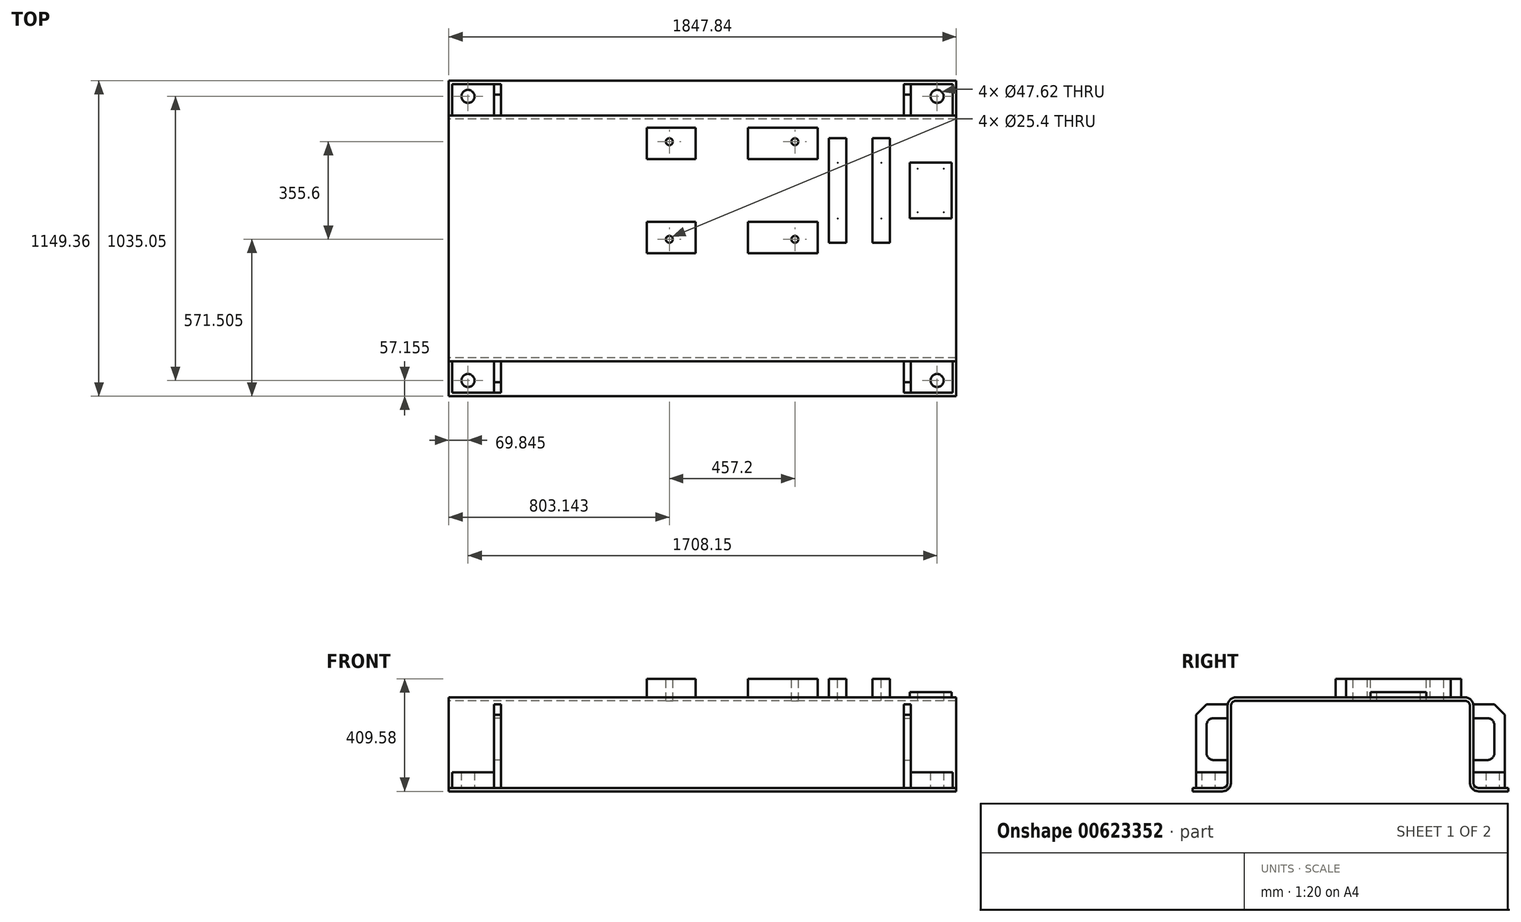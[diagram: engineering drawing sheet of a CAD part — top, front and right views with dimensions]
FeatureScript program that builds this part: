
annotation { "Feature Type Name" : "Feature", "Feature Type Description" : "" }
export const myFeature = defineFeature(function(context is Context, id is Id, definition is map)
    precondition{}
    {
        {
            var Q0;
            Q0=qCreatedBy(makeId("Right.planeOp"),FACE);
            var sketch = newSketch(context, id + "F0", { "sketchPlane" : qUnion([Q0])});
            skLineSegment(sketch, "E0.bottom", {"start": v(-415.93, 171.45) * mm, "end": v(0, 171.45) * mm});
            skLineSegment(sketch, "E0.top", {"start": v(-574.68, -171.45) * mm, "end": v(-466.73, -171.45) * mm});
            skLineSegment(sketch, "E0.left", {"start": v(-574.68, -158.75) * mm, "end": v(-574.68, -171.45) * mm});
            skPoint(sketch, "E0.middle", {"position": v(0, 0) * mm});
            skLineSegment(sketch, "E1", {"start": v(0, 352.56) * mm, "end": v(0, -350.8) * mm, "construction": true});
            skPoint(sketch, "E1.endSnap0", {"position": v(0, 171.45) * mm});
            skLineSegment(sketch, "E2.0", {"start": v(-447.68, 139.7) * mm, "end": v(-447.68, -139.7) * mm});
            skLineSegment(sketch, "E3.0", {"start": v(-574.68, -158.75) * mm, "end": v(-466.73, -158.75) * mm});
            skLineSegment(sketch, "E4.0", {"start": v(-434.98, 139.7) * mm, "end": v(-434.98, -139.7) * mm});
            skLineSegment(sketch, "E5.0", {"start": v(-415.93, 158.75) * mm, "end": v(0, 158.75) * mm});
            skArc(sketch, "E6.filletArc", {"start": v(-466.73, -158.75) * mm, "mid": v(-453.25, -153.17) * mm, "end": v(-447.68, -139.7) * mm});
            skArc(sketch, "E7.filletArc", {"start": v(-415.93, 158.75) * mm, "mid": v(-429.4, 153.17) * mm, "end": v(-434.98, 139.7) * mm});
            skPoint(sketch, "E8.newPointA", {"position": v(574.68, -171.45) * mm});
            skArc(sketch, "E8.filletArc", {"start": v(-466.73, -171.45) * mm, "mid": v(-444.27, -162.15) * mm, "end": v(-434.98, -139.7) * mm});
            skPoint(sketch, "E9.newPointB", {"position": v(-574.67, 171.45) * mm});
            skArc(sketch, "E9.filletArc", {"start": v(-415.93, 171.45) * mm, "mid": v(-438.38, 162.15) * mm, "end": v(-447.68, 139.7) * mm});
            skArc(sketch, "E10.MirrorCS", {"start": v(466.73, -158.75) * mm, "mid": v(453.25, -153.17) * mm, "end": v(447.68, -139.7) * mm});
            skArc(sketch, "E11.MirrorCS", {"start": v(415.93, 158.75) * mm, "mid": v(429.4, 153.17) * mm, "end": v(434.98, 139.7) * mm});
            skLineSegment(sketch, "E12.MirrorCS", {"start": v(574.68, -158.75) * mm, "end": v(574.68, -171.45) * mm});
            skArc(sketch, "E13.MirrorCS", {"start": v(466.73, -171.45) * mm, "mid": v(444.27, -162.15) * mm, "end": v(434.98, -139.7) * mm});
            skArc(sketch, "E14.MirrorCS", {"start": v(415.93, 171.45) * mm, "mid": v(438.38, 162.15) * mm, "end": v(447.68, 139.7) * mm});
            skLineSegment(sketch, "E15.MirrorCS", {"start": v(574.68, -171.45) * mm, "end": v(466.73, -171.45) * mm});
            skLineSegment(sketch, "E16.MirrorCS", {"start": v(574.68, -158.75) * mm, "end": v(466.73, -158.75) * mm});
            skPoint(sketch, "E17.MirrorP", {"position": v(574.68, 171.45) * mm});
            skLineSegment(sketch, "E18.MirrorCS", {"start": v(447.68, 139.7) * mm, "end": v(447.68, -139.7) * mm});
            skLineSegment(sketch, "E19.MirrorCS", {"start": v(434.98, 139.7) * mm, "end": v(434.98, -139.7) * mm});
            skLineSegment(sketch, "E20.MirrorCS", {"start": v(415.93, 158.75) * mm, "end": v(0, 158.75) * mm});
            skLineSegment(sketch, "E21.MirrorCS", {"start": v(415.93, 171.45) * mm, "end": v(0, 171.45) * mm});
            skSolve(sketch);
        }
        {
            var Q0;
            Q0 = qSketchRegion(id + "F0", true);
            extrude(context, id + "F1", {"entities" : qUnion([Q0]), "endBound" : BoundingType.SYMMETRIC, "depth" : 1847.85 * mm, "offsetDistance" : 25.4 * mm});
        }
        {
            var Q0;
            Q0=makeQuery(id+"F1.opExtrude","SWEPT_FACE",FACE,{"disambiguationData":[OSD([sQuery(id+"F0.wireOp",EDGE,"E3.0")])]});
            var sketch = newSketch(context, id + "F2", { "sketchPlane" : qUnion([Q0])});
            skLineSegment(sketch, "E22.0", {"start": v(911.23, -561.98) * mm, "end": v(911.23, -447.68) * mm});
            skLineSegment(sketch, "E23.0", {"start": v(758.83, -561.98) * mm, "end": v(758.83, -447.68) * mm});
            skLineSegment(sketch, "E24.0", {"start": v(923.93, -447.68) * mm, "end": v(758.83, -447.68) * mm});
            skLineSegment(sketch, "E25.0.1", {"start": v(758.83, -447.68) * mm, "end": v(923.93, -447.68) * mm});
            skLineSegment(sketch, "E26.0", {"start": v(911.23, -447.68) * mm, "end": v(758.83, -447.68) * mm});
            skLineSegment(sketch, "E27.0", {"start": v(911.23, -561.98) * mm, "end": v(758.83, -561.98) * mm});
            skPoint(sketch, "E28.orphan", {"position": v(-923.93, -447.68) * mm});
            skLineSegment(sketch, "E29", {"start": v(0, 247.47) * mm, "end": v(0, -268.79) * mm, "construction": true});
            skLineSegment(sketch, "E30", {"start": v(-290.88, 0) * mm, "end": v(261.25, 0) * mm, "construction": true});
            skLineSegment(sketch, "E31.0", {"start": v(854.08, 247.47) * mm, "end": v(854.08, -517.52) * mm, "construction": true});
            skLineSegment(sketch, "E32.0", {"start": v(-290.88, -517.52) * mm, "end": v(854.08, -517.52) * mm, "construction": true});
            skCircle(sketch, "E33", {"center": v(854.08, -517.52) * mm, "radius": 23.81 * mm});
            skSolve(sketch);
        }
        {
            var Q0;
            Q0 = qSketchRegion(id + "F2", true);
            extrude(context, id + "F3", {"entities" : qUnion([Q0]), "depth" : 57.15 * mm, "offsetDistance" : 25.4 * mm});
        }
        {
            var Q0;
            Q0=makeQuery(id+"F3.opExtrude","SWEPT_FACE",FACE,{"disambiguationData":[OSD([sQuery(id+"F2.wireOp",EDGE,"E23.0")])]});
            var sketch = newSketch(context, id + "F4", { "sketchPlane" : qUnion([Q0])});
            skLineSegment(sketch, "E34.bottom", {"start": v(447.68, -158.75) * mm, "end": v(561.98, -158.75) * mm});
            skLineSegment(sketch, "E34.top", {"start": v(447.67, 146.05) * mm, "end": v(561.98, 146.05) * mm});
            skLineSegment(sketch, "E34.left", {"start": v(447.68, -158.75) * mm, "end": v(447.68, -57.15) * mm});
            skLineSegment(sketch, "E34.right", {"start": v(561.98, -158.75) * mm, "end": v(561.98, 146.05) * mm});
            skLineSegment(sketch, "E35.0", {"start": v(447.67, 95.25) * mm, "end": v(498.48, 95.25) * mm});
            skLineSegment(sketch, "E36.0", {"start": v(447.67, -57.15) * mm, "end": v(498.48, -57.15) * mm});
            skLineSegment(sketch, "E37.0", {"start": v(523.88, -31.75) * mm, "end": v(523.88, 69.85) * mm});
            skArc(sketch, "E38.filletArc", {"start": v(523.88, 69.85) * mm, "mid": v(516.44, 87.81) * mm, "end": v(498.48, 95.25) * mm});
            skArc(sketch, "E39.filletArc", {"start": v(498.48, -57.15) * mm, "mid": v(516.44, -49.71) * mm, "end": v(523.88, -31.75) * mm});
            skLineSegment(sketch, "E40.trimOffspring", {"start": v(447.68, 95.25) * mm, "end": v(447.68, 146.05) * mm});
            skSolve(sketch);
        }
        {
            var Q0;
            Q0 = qSketchRegion(id + "F4", true);
            extrude(context, id + "F5", {"entities" : qUnion([Q0]), "depth" : 25.4 * mm, "offsetDistance" : 25.4 * mm});
        }
        {
            var Q0;
            Q0=makeQuery(id+"F5.opExtrude","SWEPT_EDGE",EDGE,{"disambiguationData":[OSD([sQuery(id+"F4.wireOp",EDGE,"E34.top"),sQuery(id+"F4.wireOp",EDGE,"E34.right")])]});
            chamfer(context, id + "F6", {"entities" : qUnion([Q0]), "width" : 38.1 * mm, "tangentPropagation" : true});
        }
        {
            var Q0;
            Q0=makeQuery(id+"F5.opExtrude","SWEPT_BODY",BODY,{"disambiguationData":[OSD([sQuery(id+"F4.wireOp",EDGE,"E34.bottom"),sQuery(id+"F4.wireOp",EDGE,"E34.top"),sQuery(id+"F4.wireOp",EDGE,"E34.left"),sQuery(id+"F4.wireOp",EDGE,"E34.right"),sQuery(id+"F4.wireOp",EDGE,"E35.0"),sQuery(id+"F4.wireOp",EDGE,"E36.0"),sQuery(id+"F4.wireOp",EDGE,"E37.0"),sQuery(id+"F4.wireOp",EDGE,"E38.filletArc"),sQuery(id+"F4.wireOp",EDGE,"E39.filletArc"),sQuery(id+"F4.wireOp",EDGE,"E40.trimOffspring")])]});
            var Q1;
            Q1=makeQuery(id+"F3.opExtrude","SWEPT_BODY",BODY,{"disambiguationData":[OSD([sQuery(id+"F2.wireOp",EDGE,"E22.0"),sQuery(id+"F2.wireOp",EDGE,"E23.0"),sQuery(id+"F2.wireOp",EDGE,"E26.0"),sQuery(id+"F2.wireOp",EDGE,"E27.0"),sQuery(id+"F2.wireOp",EDGE,"E33")])]});
            var Q2;
            Q2=qCreatedBy(makeId("Right.planeOp"),FACE);
            mirror(context, id + "F7", {"entities" : qUnion([Q0, Q1]), "mirrorPlane" : qUnion([Q2])});
        }
        {
            var Q0;
            Q0=makeQuery(id+"F3.opExtrude","SWEPT_BODY",BODY,{"disambiguationData":[OSD([sQuery(id+"F2.wireOp",EDGE,"E22.0"),sQuery(id+"F2.wireOp",EDGE,"E23.0"),sQuery(id+"F2.wireOp",EDGE,"E26.0"),sQuery(id+"F2.wireOp",EDGE,"E27.0"),sQuery(id+"F2.wireOp",EDGE,"E33")])]});
            var Q1;
            Q1=makeQuery(id+"F5.opExtrude","SWEPT_BODY",BODY,{"disambiguationData":[OSD([sQuery(id+"F4.wireOp",EDGE,"E34.bottom"),sQuery(id+"F4.wireOp",EDGE,"E34.top"),sQuery(id+"F4.wireOp",EDGE,"E34.left"),sQuery(id+"F4.wireOp",EDGE,"E34.right"),sQuery(id+"F4.wireOp",EDGE,"E35.0"),sQuery(id+"F4.wireOp",EDGE,"E36.0"),sQuery(id+"F4.wireOp",EDGE,"E37.0"),sQuery(id+"F4.wireOp",EDGE,"E38.filletArc"),sQuery(id+"F4.wireOp",EDGE,"E39.filletArc"),sQuery(id+"F4.wireOp",EDGE,"E40.trimOffspring")])]});
            var Q2;
            Q2=makeQuery(id+"F7.opPattern","COPY",BODY,{"derivedFrom":makeQuery(id+"F3.opExtrude","SWEPT_BODY",BODY,{"disambiguationData":[OSD([sQuery(id+"F2.wireOp",EDGE,"E22.0"),sQuery(id+"F2.wireOp",EDGE,"E23.0"),sQuery(id+"F2.wireOp",EDGE,"E26.0"),sQuery(id+"F2.wireOp",EDGE,"E27.0"),sQuery(id+"F2.wireOp",EDGE,"E33")])]}),"instanceName":"1"});
            var Q3;
            Q3=makeQuery(id+"F7.opPattern","COPY",BODY,{"derivedFrom":makeQuery(id+"F5.opExtrude","SWEPT_BODY",BODY,{"disambiguationData":[OSD([sQuery(id+"F4.wireOp",EDGE,"E34.bottom"),sQuery(id+"F4.wireOp",EDGE,"E34.top"),sQuery(id+"F4.wireOp",EDGE,"E34.left"),sQuery(id+"F4.wireOp",EDGE,"E34.right"),sQuery(id+"F4.wireOp",EDGE,"E35.0"),sQuery(id+"F4.wireOp",EDGE,"E36.0"),sQuery(id+"F4.wireOp",EDGE,"E37.0"),sQuery(id+"F4.wireOp",EDGE,"E38.filletArc"),sQuery(id+"F4.wireOp",EDGE,"E39.filletArc"),sQuery(id+"F4.wireOp",EDGE,"E40.trimOffspring")])]}),"instanceName":"1"});
            var Q4;
            Q4=qCreatedBy(makeId("Front.planeOp"),FACE);
            mirror(context, id + "F8", {"entities" : qUnion([Q0, Q1, Q2, Q3]), "mirrorPlane" : qUnion([Q4])});
        }
        {
            var Q0;
            Q0=makeQuery(id+"F1.opExtrude","SWEPT_FACE",FACE,{"disambiguationData":[OSD([sQuery(id+"F0.wireOp",EDGE,"E0.bottom"),sQuery(id+"F0.wireOp",EDGE,"E21.MirrorCS")])]});
            var sketch = newSketch(context, id + "F9", { "sketchPlane" : qUnion([Q0])});
            skLineSegment(sketch, "E41.0", {"start": v(923.93, -206.38) * mm, "end": v(-923.93, -206.38) * mm, "construction": true});
            skLineSegment(sketch, "E42.0", {"start": v(923.93, 174.62) * mm, "end": v(-923.93, 174.62) * mm, "construction": true});
            skLineSegment(sketch, "E43.0", {"start": v(-669.93, 415.93) * mm, "end": v(-669.93, -415.93) * mm, "construction": true});
            skLineSegment(sketch, "E44.0", {"start": v(107.82, 415.93) * mm, "end": v(107.82, -415.93) * mm, "construction": true});
            skLineSegment(sketch, "E45.0", {"start": v(571.37, 415.93) * mm, "end": v(571.37, -415.93) * mm, "construction": true});
            skLineSegment(sketch, "E46.0", {"start": v(830.96, 415.93) * mm, "end": v(830.96, -415.93) * mm, "construction": true});
            skLineSegment(sketch, "E47.bottom", {"start": v(754.76, 276.23) * mm, "end": v(907.16, 276.23) * mm});
            skLineSegment(sketch, "E47.top", {"start": v(754.76, 73.02) * mm, "end": v(907.16, 73.02) * mm});
            skLineSegment(sketch, "E47.left", {"start": v(754.76, 276.23) * mm, "end": v(754.76, 73.02) * mm});
            skLineSegment(sketch, "E47.right", {"start": v(907.16, 276.23) * mm, "end": v(907.16, 73.02) * mm});
            skPoint(sketch, "E47.middle", {"position": v(830.96, 174.62) * mm});
            skSolve(sketch);
        }
        {
            var Q0;
            Q0 = qSketchRegion(id + "F9", true);
            extrude(context, id + "F10", {"entities" : qUnion([Q0]), "operationType" : NewBodyOperationType.ADD, "depth" : 19.05 * mm, "offsetDistance" : 25.4 * mm});
        }
        {
            var Q0;
            Q0=makeQuery(id+"F10.opExtrude","CAP_FACE",FACE,{"disambiguationData":[OSD([sQuery(id+"F9.wireOp",EDGE,"E47.bottom"),sQuery(id+"F9.wireOp",EDGE,"E47.top"),sQuery(id+"F9.wireOp",EDGE,"E47.left"),sQuery(id+"F9.wireOp",EDGE,"E47.right")])],"isStart":false});
            var sketch = newSketch(context, id + "F11", { "sketchPlane" : qUnion([Q0])});
            skLineSegment(sketch, "E48.0", {"start": v(830.96, 415.93) * mm, "end": v(830.96, -415.93) * mm, "construction": true});
            skLineSegment(sketch, "E49.0", {"start": v(923.93, 174.62) * mm, "end": v(-923.93, 174.62) * mm, "construction": true});
            skLineSegment(sketch, "E50.bottom", {"start": v(783.34, 254) * mm, "end": v(878.59, 254) * mm, "construction": true});
            skLineSegment(sketch, "E50.top", {"start": v(783.34, 95.25) * mm, "end": v(878.59, 95.25) * mm, "construction": true});
            skLineSegment(sketch, "E50.left", {"start": v(783.34, 254) * mm, "end": v(783.34, 95.25) * mm, "construction": true});
            skLineSegment(sketch, "E50.right", {"start": v(878.59, 254) * mm, "end": v(878.59, 95.25) * mm, "construction": true});
            skPoint(sketch, "E50.middle", {"position": v(830.96, 174.62) * mm});
            skPoint(sketch, "E51", {"position": v(783.34, 254) * mm});
            skPoint(sketch, "E52", {"position": v(878.59, 254) * mm});
            skPoint(sketch, "E53", {"position": v(878.59, 95.25) * mm});
            skPoint(sketch, "E54", {"position": v(783.34, 95.25) * mm});
            skSolve(sketch);
        }
        {
            var Q0;
            Q0=sQuery(id+"F11.wireOp",VERTEX,"E51");
            var Q1;
            Q1=sQuery(id+"F11.wireOp",VERTEX,"E52");
            var Q2;
            Q2=sQuery(id+"F11.wireOp",VERTEX,"E54");
            var Q3;
            Q3=sQuery(id+"F11.wireOp",VERTEX,"E53");
            var Q4;
            Q4=makeQuery(id+"F1.opExtrude","SWEPT_BODY",BODY,{"disambiguationData":[OSD([sQuery(id+"F0.wireOp",EDGE,"E0.bottom"),sQuery(id+"F0.wireOp",EDGE,"E0.top"),sQuery(id+"F0.wireOp",EDGE,"E0.left"),sQuery(id+"F0.wireOp",EDGE,"E2.0"),sQuery(id+"F0.wireOp",EDGE,"E3.0"),sQuery(id+"F0.wireOp",EDGE,"E4.0"),sQuery(id+"F0.wireOp",EDGE,"E5.0"),sQuery(id+"F0.wireOp",EDGE,"E6.filletArc"),sQuery(id+"F0.wireOp",EDGE,"E7.filletArc"),sQuery(id+"F0.wireOp",EDGE,"E8.filletArc"),sQuery(id+"F0.wireOp",EDGE,"E9.filletArc"),sQuery(id+"F0.wireOp",EDGE,"E10.MirrorCS"),sQuery(id+"F0.wireOp",EDGE,"E11.MirrorCS"),sQuery(id+"F0.wireOp",EDGE,"E12.MirrorCS"),sQuery(id+"F0.wireOp",EDGE,"E13.MirrorCS"),sQuery(id+"F0.wireOp",EDGE,"E14.MirrorCS"),sQuery(id+"F0.wireOp",EDGE,"E15.MirrorCS"),sQuery(id+"F0.wireOp",EDGE,"E16.MirrorCS"),sQuery(id+"F0.wireOp",EDGE,"E18.MirrorCS"),sQuery(id+"F0.wireOp",EDGE,"E19.MirrorCS"),sQuery(id+"F0.wireOp",EDGE,"E20.MirrorCS"),sQuery(id+"F0.wireOp",EDGE,"E21.MirrorCS")])]});
            hole(context, id + "F12", {"style" : HoleStyle.SIMPLE, "endStyle" : HoleEndStyle.THROUGH, "standardTappedOrClearance" : lookupTablePath({ "standard" : "ANSI", "size" : "9/16 (0.56)", "type" : "Drilled" }), "standardBlindInLast" : lookupTablePath({ "standard" : "ANSI", "size" : "9/16", "type" : "Drilled" }), "holeDiameter" : 9 / 406.4 * mm, "majorDiameter" : 6.35 * mm, "isTappedThrough" : true, "tappedDepth" : 15.24 * mm, "tapClearance" : 3, "locations" : qUnion([Q0, Q1, Q2, Q3]), "scope" : qUnion([Q4])});
        }
        {
            var Q0;
            Q0=makeQuery(id+"F9.imprint","IMPRINT",FACE,{"disambiguationData":[TD([[makeQuery(id+"F9.imprint","IMPRINT",EDGE,{"derivedFrom":sQuery(id+"F9.wireOp",EDGE,"E47.bottom")}),1.0]])]});
            var sketch = newSketch(context, id + "F13", { "sketchPlane" : qUnion([Q0])});
            skLineSegment(sketch, "E55.0", {"start": v(571.37, 415.93) * mm, "end": v(571.37, -415.93) * mm, "construction": true});
            skLineSegment(sketch, "E56.0", {"start": v(523.75, 365.13) * mm, "end": v(523.75, 174.62) * mm});
            skLineSegment(sketch, "E57.0", {"start": v(460.25, 365.13) * mm, "end": v(460.25, 174.62) * mm});
            skLineSegment(sketch, "E58.trimOffspring", {"start": v(523.75, 365.13) * mm, "end": v(460.25, 365.13) * mm});
            skLineSegment(sketch, "E59.0", {"start": v(923.93, 174.62) * mm, "end": v(-923.93, 174.62) * mm, "construction": true});
            skLineSegment(sketch, "E60.MirrorCS", {"start": v(523.75, -15.88) * mm, "end": v(523.75, 174.62) * mm});
            skLineSegment(sketch, "E61.MirrorCS", {"start": v(460.25, -15.88) * mm, "end": v(460.25, 174.62) * mm});
            skLineSegment(sketch, "E62.MirrorCS", {"start": v(523.75, -15.88) * mm, "end": v(460.25, -15.88) * mm});
            skLineSegment(sketch, "E63.MirrorCS", {"start": v(619, 365.13) * mm, "end": v(682.5, 365.13) * mm});
            skLineSegment(sketch, "E64.MirrorCS", {"start": v(619, 365.13) * mm, "end": v(619, 174.62) * mm});
            skLineSegment(sketch, "E65.MirrorCS", {"start": v(682.5, 365.13) * mm, "end": v(682.5, 174.62) * mm});
            skLineSegment(sketch, "E66.MirrorCS", {"start": v(619, -15.88) * mm, "end": v(619, 174.62) * mm});
            skLineSegment(sketch, "E67.MirrorCS", {"start": v(682.5, -15.88) * mm, "end": v(682.5, 174.62) * mm});
            skLineSegment(sketch, "E68.MirrorCS", {"start": v(619, -15.88) * mm, "end": v(682.5, -15.88) * mm});
            skSolve(sketch);
        }
        {
            var Q0;
            Q0=makeQuery(id+"F13.imprint","IMPRINT",FACE,{"disambiguationData":[TD([[makeQuery(id+"F13.imprint","IMPRINT",EDGE,{"derivedFrom":sQuery(id+"F13.wireOp",EDGE,"E56.0")}),-1.0]])]});
            var Q1;
            Q1=makeQuery(id+"F13.imprint","IMPRINT",FACE,{"disambiguationData":[TD([[makeQuery(id+"F13.imprint","IMPRINT",EDGE,{"derivedFrom":sQuery(id+"F13.wireOp",EDGE,"E63.MirrorCS")}),-1.0]])]});
            extrude(context, id + "F14", {"entities" : qUnion([Q0, Q1]), "operationType" : NewBodyOperationType.ADD, "depth" : 66.55 * mm, "offsetDistance" : 25.4 * mm});
        }
        {
            var Q0;
            Q0=makeQuery(id+"F14.opExtrude","CAP_FACE",FACE,{"disambiguationData":[OSD([sQuery(id+"F13.wireOp",EDGE,"E56.0"),sQuery(id+"F13.wireOp",EDGE,"E57.0"),sQuery(id+"F13.wireOp",EDGE,"E58.trimOffspring"),sQuery(id+"F13.wireOp",EDGE,"E60.MirrorCS"),sQuery(id+"F13.wireOp",EDGE,"E61.MirrorCS"),sQuery(id+"F13.wireOp",EDGE,"E62.MirrorCS")])],"isStart":false});
            var sketch = newSketch(context, id + "F15", { "sketchPlane" : qUnion([Q0])});
            skLineSegment(sketch, "E69.0", {"start": v(571.37, 415.93) * mm, "end": v(571.37, -415.93) * mm, "construction": true});
            skLineSegment(sketch, "E70.0", {"start": v(923.93, 174.62) * mm, "end": v(-923.93, 174.62) * mm, "construction": true});
            skLineSegment(sketch, "E71.0", {"start": v(492, 415.93) * mm, "end": v(492, -415.93) * mm, "construction": true});
            skLineSegment(sketch, "E72.0", {"start": v(923.93, 276.23) * mm, "end": v(-923.93, 276.23) * mm, "construction": true});
            skPoint(sketch, "E73", {"position": v(492, 276.23) * mm});
            skPoint(sketch, "E74.0.1.0", {"position": v(492, 73.02) * mm});
            skPoint(sketch, "E74.1.0.0", {"position": v(650.75, 276.23) * mm});
            skPoint(sketch, "E74.1.1.0", {"position": v(650.75, 73.02) * mm});
            skLineSegment(sketch, "E74.direction1", {"start": v(492, 276.23) * mm, "end": v(650.75, 276.23) * mm, "construction": true});
            skLineSegment(sketch, "E74.direction2", {"start": v(492, 276.23) * mm, "end": v(492, 73.02) * mm, "construction": true});
            skSolve(sketch);
        }
        {
            var Q0;
            Q0=sQuery(id+"F15.wireOp",VERTEX,"E73");
            var Q1;
            Q1=sQuery(id+"F15.wireOp",VERTEX,"E74.1.0.0");
            var Q2;
            Q2=sQuery(id+"F15.wireOp",VERTEX,"E74.0.1.0");
            var Q3;
            Q3=sQuery(id+"F15.wireOp",VERTEX,"E74.1.1.0");
            var Q4;
            Q4=makeQuery(id+"F1.opExtrude","SWEPT_BODY",BODY,{"disambiguationData":[OSD([sQuery(id+"F0.wireOp",EDGE,"E0.bottom"),sQuery(id+"F0.wireOp",EDGE,"E0.top"),sQuery(id+"F0.wireOp",EDGE,"E0.left"),sQuery(id+"F0.wireOp",EDGE,"E2.0"),sQuery(id+"F0.wireOp",EDGE,"E3.0"),sQuery(id+"F0.wireOp",EDGE,"E4.0"),sQuery(id+"F0.wireOp",EDGE,"E5.0"),sQuery(id+"F0.wireOp",EDGE,"E6.filletArc"),sQuery(id+"F0.wireOp",EDGE,"E7.filletArc"),sQuery(id+"F0.wireOp",EDGE,"E8.filletArc"),sQuery(id+"F0.wireOp",EDGE,"E9.filletArc"),sQuery(id+"F0.wireOp",EDGE,"E10.MirrorCS"),sQuery(id+"F0.wireOp",EDGE,"E11.MirrorCS"),sQuery(id+"F0.wireOp",EDGE,"E12.MirrorCS"),sQuery(id+"F0.wireOp",EDGE,"E13.MirrorCS"),sQuery(id+"F0.wireOp",EDGE,"E14.MirrorCS"),sQuery(id+"F0.wireOp",EDGE,"E15.MirrorCS"),sQuery(id+"F0.wireOp",EDGE,"E16.MirrorCS"),sQuery(id+"F0.wireOp",EDGE,"E18.MirrorCS"),sQuery(id+"F0.wireOp",EDGE,"E19.MirrorCS"),sQuery(id+"F0.wireOp",EDGE,"E20.MirrorCS"),sQuery(id+"F0.wireOp",EDGE,"E21.MirrorCS")])]});
            hole(context, id + "F16", {"style" : HoleStyle.SIMPLE, "endStyle" : HoleEndStyle.THROUGH, "standardTappedOrClearance" : lookupTablePath({ "standard" : "ANSI", "size" : "11/16 (0.69)", "type" : "Drilled" }), "standardBlindInLast" : lookupTablePath({ "standard" : "ANSI", "size" : "11/16", "type" : "Drilled" }), "holeDiameter" : 11 / 406.4 * mm, "majorDiameter" : 6.35 * mm, "isTappedThrough" : true, "tappedDepth" : 15.24 * mm, "tapClearance" : 3, "locations" : qUnion([Q0, Q1, Q2, Q3]), "scope" : qUnion([Q4])});
        }
        {
            var Q0;
            Q0=makeQuery(id+"F9.imprint","IMPRINT",FACE,{"disambiguationData":[TD([[makeQuery(id+"F9.imprint","IMPRINT",EDGE,{"derivedFrom":sQuery(id+"F9.wireOp",EDGE,"E47.bottom")}),1.0]])]});
            var sketch = newSketch(context, id + "F17", { "sketchPlane" : qUnion([Q0])});
            skLineSegment(sketch, "E75.0", {"start": v(-25.53, 60.32) * mm, "end": v(-25.53, -53.98) * mm});
            skLineSegment(sketch, "E76.0", {"start": v(-203.33, 60.32) * mm, "end": v(-203.33, -53.98) * mm});
            skLineSegment(sketch, "E77.0", {"start": v(-25.53, 60.32) * mm, "end": v(-203.33, 60.32) * mm});
            skLineSegment(sketch, "E78.0", {"start": v(-25.53, -53.98) * mm, "end": v(-203.33, -53.98) * mm});
            skLineSegment(sketch, "E79.MirrorCS", {"start": v(-25.53, 288.93) * mm, "end": v(-203.33, 288.93) * mm});
            skLineSegment(sketch, "E80.MirrorCS", {"start": v(-203.33, 288.93) * mm, "end": v(-203.33, 403.23) * mm});
            skLineSegment(sketch, "E81.MirrorCS", {"start": v(-25.53, 403.23) * mm, "end": v(-203.33, 403.23) * mm});
            skLineSegment(sketch, "E82.MirrorCS", {"start": v(-25.53, 288.93) * mm, "end": v(-25.53, 403.23) * mm});
            skLineSegment(sketch, "E83.MirrorCS", {"start": v(418.97, 288.93) * mm, "end": v(418.97, 403.23) * mm});
            skLineSegment(sketch, "E84.MirrorCS", {"start": v(164.97, 403.23) * mm, "end": v(418.97, 403.23) * mm});
            skLineSegment(sketch, "E85.MirrorCS", {"start": v(164.97, 288.93) * mm, "end": v(418.97, 288.93) * mm});
            skLineSegment(sketch, "E86.MirrorCS", {"start": v(164.97, 60.32) * mm, "end": v(418.97, 60.32) * mm});
            skLineSegment(sketch, "E87.MirrorCS", {"start": v(418.97, 60.32) * mm, "end": v(418.97, -53.98) * mm});
            skLineSegment(sketch, "E88.MirrorCS", {"start": v(164.97, -53.98) * mm, "end": v(418.97, -53.98) * mm});
            skLineSegment(sketch, "E89.0", {"start": v(164.97, -53.98) * mm, "end": v(164.97, 60.32) * mm});
            skPoint(sketch, "E90.orphan", {"position": v(241.17, -53.98) * mm});
            skPoint(sketch, "E91.orphan", {"position": v(241.17, 60.32) * mm});
            skPoint(sketch, "E92.orphan", {"position": v(241.17, 288.93) * mm});
            skPoint(sketch, "E93.orphan", {"position": v(241.17, 403.23) * mm});
            skLineSegment(sketch, "E94.trimOffspring", {"start": v(164.97, 288.93) * mm, "end": v(164.97, 403.23) * mm});
            skSolve(sketch);
        }
        {
            var Q0;
            Q0 = qSketchRegion(id + "F17", true);
            extrude(context, id + "F18", {"entities" : qUnion([Q0]), "operationType" : NewBodyOperationType.ADD, "depth" : 66.67 * mm, "offsetDistance" : 25.4 * mm});
        }
        {
            var Q0;
            Q0=makeQuery(id+"F18.opExtrude","CAP_FACE",FACE,{"disambiguationData":[OSD([sQuery(id+"F17.wireOp",EDGE,"E83.MirrorCS"),sQuery(id+"F17.wireOp",EDGE,"E84.MirrorCS"),sQuery(id+"F17.wireOp",EDGE,"E85.MirrorCS"),sQuery(id+"F17.wireOp",EDGE,"E94.trimOffspring")])],"isStart":false});
            var sketch = newSketch(context, id + "F19", { "sketchPlane" : qUnion([Q0])});
            skLineSegment(sketch, "E95.0", {"start": v(107.82, 415.93) * mm, "end": v(107.82, -415.93) * mm, "construction": true});
            skLineSegment(sketch, "E96.0", {"start": v(923.93, 174.62) * mm, "end": v(-923.93, 174.62) * mm, "construction": true});
            skLineSegment(sketch, "E97.0", {"start": v(-120.78, 415.93) * mm, "end": v(-120.78, -415.93) * mm, "construction": true});
            skLineSegment(sketch, "E98.0", {"start": v(923.93, 352.43) * mm, "end": v(-923.93, 352.43) * mm, "construction": true});
            skPoint(sketch, "E99", {"position": v(-120.78, 352.43) * mm});
            skPoint(sketch, "E100.MirrorP", {"position": v(336.42, 352.43) * mm});
            skPoint(sketch, "E101.MirrorP", {"position": v(-120.78, -3.18) * mm});
            skPoint(sketch, "E102.MirrorP", {"position": v(336.42, -3.18) * mm});
            skSolve(sketch);
        }
        {
            var Q0;
            Q0=sQuery(id+"F19.wireOp",VERTEX,"E99");
            var Q1;
            Q1=sQuery(id+"F19.wireOp",VERTEX,"E100.MirrorP");
            var Q2;
            Q2=sQuery(id+"F19.wireOp",VERTEX,"E101.MirrorP");
            var Q3;
            Q3=sQuery(id+"F19.wireOp",VERTEX,"E102.MirrorP");
            var Q4;
            Q4=makeQuery(id+"F1.opExtrude","SWEPT_BODY",BODY,{"disambiguationData":[OSD([sQuery(id+"F0.wireOp",EDGE,"E0.bottom"),sQuery(id+"F0.wireOp",EDGE,"E0.top"),sQuery(id+"F0.wireOp",EDGE,"E0.left"),sQuery(id+"F0.wireOp",EDGE,"E2.0"),sQuery(id+"F0.wireOp",EDGE,"E3.0"),sQuery(id+"F0.wireOp",EDGE,"E4.0"),sQuery(id+"F0.wireOp",EDGE,"E5.0"),sQuery(id+"F0.wireOp",EDGE,"E6.filletArc"),sQuery(id+"F0.wireOp",EDGE,"E7.filletArc"),sQuery(id+"F0.wireOp",EDGE,"E8.filletArc"),sQuery(id+"F0.wireOp",EDGE,"E9.filletArc"),sQuery(id+"F0.wireOp",EDGE,"E10.MirrorCS"),sQuery(id+"F0.wireOp",EDGE,"E11.MirrorCS"),sQuery(id+"F0.wireOp",EDGE,"E12.MirrorCS"),sQuery(id+"F0.wireOp",EDGE,"E13.MirrorCS"),sQuery(id+"F0.wireOp",EDGE,"E14.MirrorCS"),sQuery(id+"F0.wireOp",EDGE,"E15.MirrorCS"),sQuery(id+"F0.wireOp",EDGE,"E16.MirrorCS"),sQuery(id+"F0.wireOp",EDGE,"E18.MirrorCS"),sQuery(id+"F0.wireOp",EDGE,"E19.MirrorCS"),sQuery(id+"F0.wireOp",EDGE,"E20.MirrorCS"),sQuery(id+"F0.wireOp",EDGE,"E21.MirrorCS")])]});
            hole(context, id + "F20", {"style" : HoleStyle.SIMPLE, "endStyle" : HoleEndStyle.THROUGH, "standardTappedOrClearance" : lookupTablePath({ "standard" : "ANSI", "size" : "1 (1)", "type" : "Drilled" }), "standardBlindInLast" : lookupTablePath({ "standard" : "ANSI", "size" : "1", "type" : "Drilled" }), "holeDiameter" : 25.4 * mm, "majorDiameter" : 6.35 * mm, "isTappedThrough" : true, "tappedDepth" : 15.24 * mm, "tapClearance" : 3, "locations" : qUnion([Q0, Q1, Q2, Q3]), "scope" : qUnion([Q4])});
        }
    });
